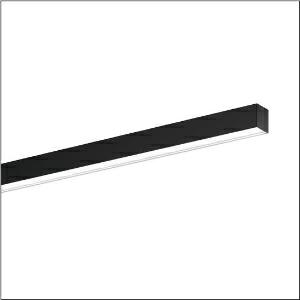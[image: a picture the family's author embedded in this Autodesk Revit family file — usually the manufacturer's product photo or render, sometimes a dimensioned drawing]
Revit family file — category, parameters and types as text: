
# Revit family: silica_r__21_51mx23da34bb_8ce5
name_source: partatom
category: Lighting Fixtures
units: mm (PartAtom-declared; Revit-internal decimal feet)

## family parameters
Cut with Voids When Loaded = No
Host = Face
Light Source = No
Part Type = Normal
Room Calculation Point = No
Round Connector Dimension = Use Diameter
Shared = No

## types (1)
- --- (1 x LED, 3280 lm, 24.1 W, 3000K)
    Apparent Load = 24 VA
    CIE Flux Codes = 78 96 99 100 100
    Color Rendering = 80
    Color Temperature = 3000K
    Default Elevation = 1800 mm
    Description = Silica® 21, office luminaire, primary optical cover: prismatic diffuser, of PMMA, CAT 2 (L<= 3000cd/m²), light emission: direct distribution, primary light characteristic: symmetric, installation type: surface-mounted, LED, rated luminous flux: 3.280lm, luminous efficacy: 136lm/W, light colour: 830, colour temperature: 3000K, with terminal, 3+2-pole, max. 2.5mm², mains connection: 220..240V, AC, 50/60Hz, rated input power: 24.1W, luminaire housing, of aluminium, jet black (RAL 9005), length: 1.204mm, width: 53mm, height: 53mm, protection rating (complete): IP20, insulation class (complete): insulation class I (protective earthing), certification: CE, permissible operating ambient temperature: 0..+35°C, standard: EN 50419, packaging unit: 1 piece
    Height = 0 mm  [stored 0 ft]
    Lamp = 1 x LED
    Lamp Light Flux = 3280 lm
    Lamp Power = 24.1 W
    Lamp count = 1
    Length = 1204 mm
    Luminous efficacy = 136 lm/W
    Manufacturer = Siteco
    ModVariant = No
    Model = 51MX23DA34BB
    Mounting Place = Ceiling
    Mounting Type = Recessed
    Number of Poles = 1
    OnlyDefault = Yes
    Power Factor = 1
    Product Name = Silica® 21
    Product group = office luminaire | ceiling recessed
    ProductGroupID = 401
    Protection Class = Protection class I
    Protection Degree = IP 20
    RLX_Detail_Level = 1
    RLX_Emergency_Light_Flux = 0 lm
    RLX_Emergency_Type = 0
    RLX_Emergency_Type_DB = No
    RlxData = <blob elided: 23717 chars, md5=8406b7a2>
    Socket = socket
    Standby Power = 0 W
    System Light Flux = 3280 lm
    System Power = 24 W
    Type Comments = factory setting: luminous flux: 100 % | dim-lin: 254 | 345 mA
    Type Image = l_1297760.jpg
    URL = http://relux.com
    VarID = @adj_049991
    Voltage = 0 V
    Weight = 0.00 kg
    Width = 53 mm

note: [stored X ft] marks values corroborated as IEEE doubles in the binary element streams (Revit-internal decimal feet)

## geometry (parser evidence)
native form markers: Blend x4, Sweep x10
no freeform markers — native parametric forms only
